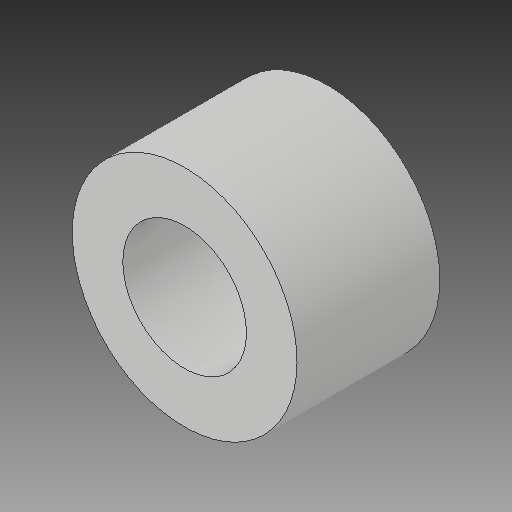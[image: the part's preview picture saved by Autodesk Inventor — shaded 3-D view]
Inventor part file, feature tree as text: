
AUTODESK INVENTOR PART (.ipt)
format: ipt  version: 2018 (Build 220112000, 112)  size: 101,888 bytes
history: native  units: mm
features: other x3, sketch x1
ambient origin geometry x8: Origin, YZ Plane, XZ Plane, XY Plane, X Axis, Y Axis, Z Axis, Center Point
bodies: Solid1 (feature_tree)
feature tree (4):
  other  "Small-Aluminium-Spacer.ipt"
  other  "Solid1::Small-Aluminium-Spacer.ipt"
  other  "TaggingFeature1"
  sketch  "Sketch1"  dims[d0=10.0mm]
